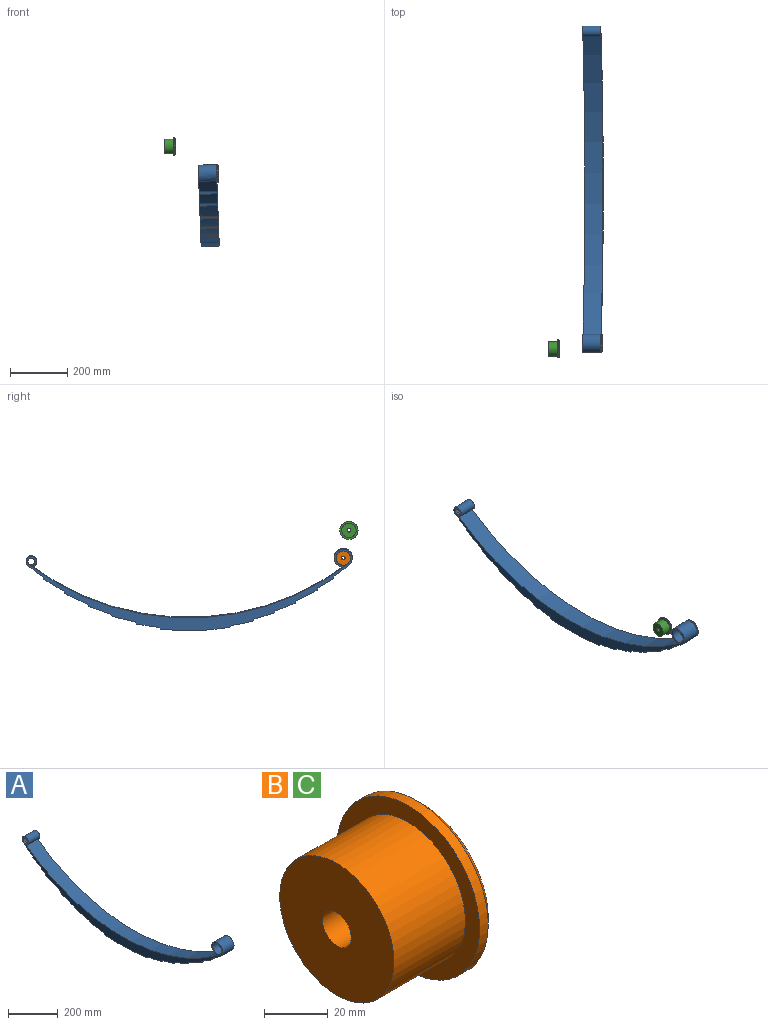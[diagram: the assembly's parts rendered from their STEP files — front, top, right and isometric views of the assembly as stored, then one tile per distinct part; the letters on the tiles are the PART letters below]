
ASSEMBLY  parts=3 mates=1
PART A: 34 faces, bbox 63.5x1143x285.8 mm
  f0: cylinder r=958.97mm len=78.52mm, axis (1,0,0), area 5042.1mm2, adj f1,f31,f32,f33
  f1: plane 63.5x7.44mm, normal (0,0.83,-0.56), area 569.3mm2, adj f0,f2,f32,f33
  f2: cylinder r=952.62mm len=80.21mm, axis (1,0,0), area 5244mm2, adj f1,f3,f32,f33
  f3: plane 63.5x7.88mm, normal (0,0.88,-0.48), area 569.3mm2, adj f2,f4,f32,f33
  f4: cylinder r=946.27mm len=78.03mm, axis (1,0,0), area 5244mm2, adj f3,f5,f32,f33
  f5: plane 63.5x8.24mm, normal (0,0.92,-0.39), area 569.3mm2, adj f4,f6,f32,f33
  f6: cylinder r=939.92mm len=80.8mm, axis (1,0,0), area 5647.7mm2, adj f5,f7,f32,f33
  f7: plane 63.5x8.56mm, normal (0,0.95,-0.3), area 569.3mm2, adj f6,f8,f32,f33
  f8: cylinder r=933.57mm len=71.29mm, axis (1,0,0), area 5244.1mm2, adj f7,f9,f32,f33
  f9: plane 63.5x8.77mm, normal (0,0.98,-0.21), area 569.3mm2, adj f8,f10,f32,f33
  f10: cylinder r=927.22mm len=63.5mm, axis (1,0,0), area 4033mm2, adj f9,f11,f32,f33
  f11: cylinder r=19.05mm len=63.5mm, axis (1,0,0), area 6370.2mm2, adj f10,f12,f32,f33
  f12: cylinder r=918.33mm len=63.5mm, axis (1,0,0), area 542.4mm2, adj f11,f13,f32,f33
  f13: cylinder r=12.7mm len=63.5mm, axis (1,0,0), area 4544.7mm2, adj f12,f14,f32,f33
  f14: cylinder r=920.87mm len=1115.3mm, axis (1,0,0), area 76073.9mm2, adj f13,f15,f32,f33
  f15: cylinder r=25.4mm len=63.5mm, axis (1,0,0), area 9396.8mm2, adj f14,f16,f32,f33
  f16: cylinder r=918.33mm len=63.5mm, axis (1,0,0), area 704.9mm2, adj f15,f17,f32,f33
  f17: cylinder r=31.75mm len=63.5mm, axis (1,0,0), area 11096.7mm2, adj f16,f18,f32,f33
  f18: cylinder r=927.22mm len=63.5mm, axis (1,0,0), area 4033mm2, adj f17,f19,f32,f33
  f19: plane 63.5x8.78mm, normal (0,-0.98,-0.2), area 569.3mm2, adj f18,f20,f32,f33
  f20: cylinder r=933.57mm len=63.5mm, axis (1,0,0), area 4033.3mm2, adj f19,f21,f32,f33
  f21: plane 63.5x8.62mm, normal (0,-0.96,-0.27), area 569.3mm2, adj f20,f22,f32,f33
  f22: cylinder r=939.92mm len=74.02mm, axis (1,0,0), area 5244mm2, adj f21,f23,f32,f33
  f23: plane 63.5x8.35mm, normal (0,-0.93,-0.36), area 569.3mm2, adj f22,f24,f32,f33
  f24: cylinder r=946.27mm len=71.11mm, axis (1,0,0), area 4840.4mm2, adj f23,f25,f32,f33
  f25: plane 63.5x8.04mm, normal (0,-0.9,-0.44), area 569.3mm2, adj f24,f26,f32,f33
  f26: cylinder r=952.62mm len=70.13mm, axis (1,0,0), area 4638.5mm2, adj f25,f27,f32,f33
  f27: plane 63.5x7.68mm, normal (0,-0.86,-0.52), area 569.3mm2, adj f26,f28,f32,f33
  f28: cylinder r=958.97mm len=74.72mm, axis (1,0,0), area 4840.3mm2, adj f27,f29,f32,f33
  f29: plane 63.5x7.25mm, normal (0,-0.81,-0.59), area 569.3mm2, adj f28,f30,f32,f33
  f30: cylinder r=965.32mm len=241.8mm, axis (1,0,0), area 15399.6mm2, adj f29,f31,f32,f33
  f31: plane 63.5x6.97mm, normal (0,0.78,-0.63), area 569.3mm2, adj f0,f30,f32,f33
  f32: plane 1143x285.75mm, normal (-1,0,0), area 34528.3mm2, adj f0,f1,f2,f3,f4,f5,f6,f7
  f33: plane 1143x285.75mm, normal (1,0,0), area 34528.3mm2, adj f0,f1,f2,f3,f4,f5,f6,f7
PART B: 7 faces, bbox 38.1x63.5x63.5 mm
  f0: cylinder r=25.4mm len=50.8mm, axis (1,0,0), area 5067.1mm2, adj f1,f4
  f1: plane 50.8x50.8mm, normal (-1,0,0), area 1900.2mm2, adj f0,f6
  f2: cylinder r=31.75mm len=63.5mm, axis (-1,0,0), area 760.1mm2, adj f4,f5
  f3: plane 58.42x58.42mm, normal (1,0,0), area 2553.8mm2, adj f5,f6
  f4: plane 63.5x63.5mm, normal (-1,0,0), area 1140.1mm2, adj f0,f2
  f5: cone r=29.21mm half-angle=45deg, axis (-1,0,0), area 687.9mm2, adj f2,f3
  f6: cylinder r=6.35mm len=38.1mm, axis (1,0,0), area 1520.1mm2, adj f1,f3
PART C: same geometry as B
PLACE A rot(axis=(0,-1,0),2.1deg) t=(-153.6,6.3,54.19)mm
PLACE B rot(axis=(0,-1,0),2.1deg) t=(-157.72,-533.45,165.24)mm
PLACE C t=(-307.65,-553.21,260.38)mm
MATE slider A.f15 <-> B.f2  axis (1,0,0.04) through (-157.72,-533.45,165.24)mm
